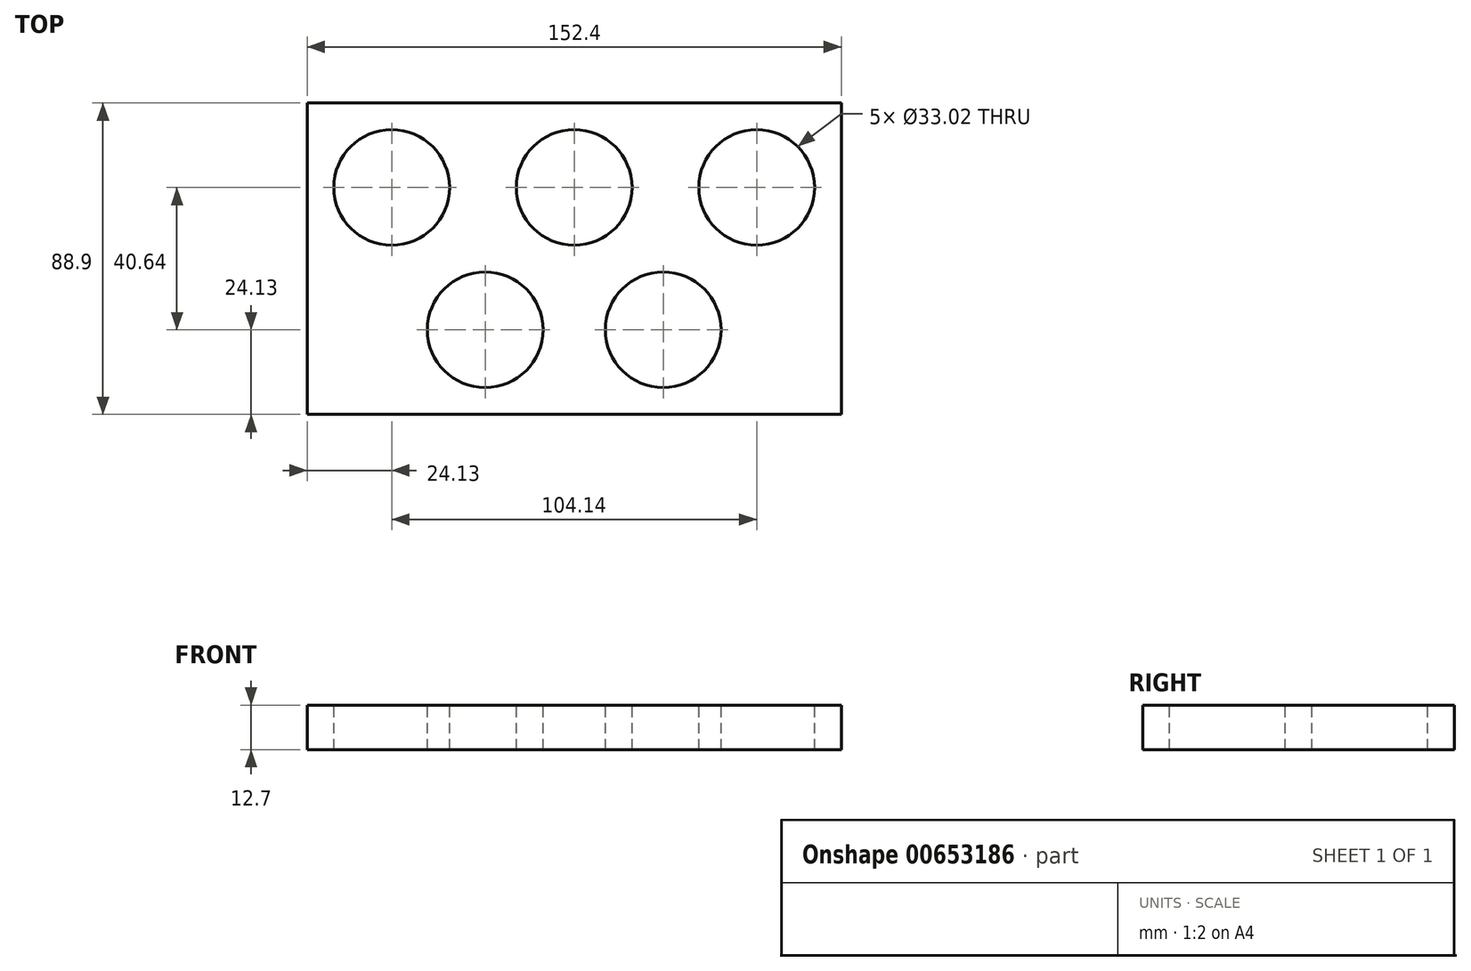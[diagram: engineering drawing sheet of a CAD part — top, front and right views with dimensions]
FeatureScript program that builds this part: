
annotation { "Feature Type Name" : "Feature", "Feature Type Description" : "" }
export const myFeature = defineFeature(function(context is Context, id is Id, definition is map)
    precondition{}
    {
        {
            var Q0;
            Q0=qCreatedBy(makeId("Top.planeOp"),FACE);
            var sketch = newSketch(context, id + "F0", { "sketchPlane" : qUnion([Q0])});
            skLineSegment(sketch, "E0.bottom", {"start": v(-76.2, -44.45) * mm, "end": v(76.2, -44.45) * mm});
            skLineSegment(sketch, "E0.top", {"start": v(-76.2, 44.45) * mm, "end": v(76.2, 44.45) * mm});
            skLineSegment(sketch, "E0.left", {"start": v(-76.2, -44.45) * mm, "end": v(-76.2, 44.45) * mm});
            skLineSegment(sketch, "E0.right", {"start": v(76.2, -44.45) * mm, "end": v(76.2, 44.45) * mm});
            skPoint(sketch, "E0.middle", {"position": v(0, 0) * mm});
            skCircle(sketch, "E1", {"center": v(-52.07, 20.32) * mm, "radius": 16.51 * mm});
            skCircle(sketch, "E2", {"center": v(0, 20.32) * mm, "radius": 16.51 * mm});
            skCircle(sketch, "E3", {"center": v(52.07, 20.32) * mm, "radius": 16.51 * mm});
            skCircle(sketch, "E4", {"center": v(-25.4, -20.32) * mm, "radius": 16.51 * mm});
            skCircle(sketch, "E5", {"center": v(25.4, -20.32) * mm, "radius": 16.51 * mm});
            skSolve(sketch);
        }
        {
            var Q0;
            Q0=makeQuery(id+"F0.imprint","IMPRINT",FACE,{"disambiguationData":[TD([[makeQuery(id+"F0.imprint","IMPRINT",EDGE,{"derivedFrom":sQuery(id+"F0.wireOp",EDGE,"E0.bottom")}),1.0]])]});
            extrude(context, id + "F1", {"entities" : qUnion([Q0]), "oppositeDirection" : true, "depth" : 12.7 * mm, "offsetDistance" : 25.4 * mm});
        }
    });
